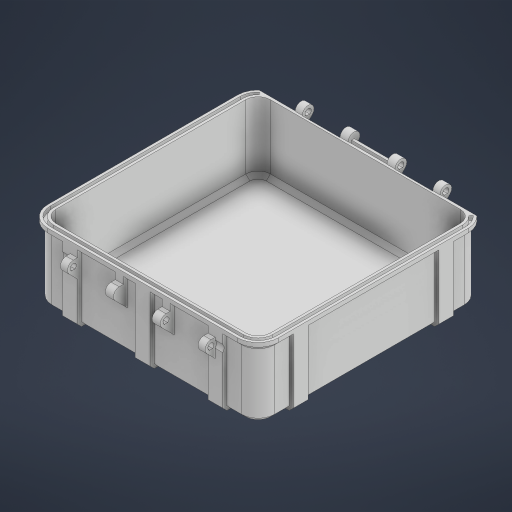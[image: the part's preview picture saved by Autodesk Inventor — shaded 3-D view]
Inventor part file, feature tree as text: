
AUTODESK INVENTOR PART (.ipt)
format: ipt  version: 2024 (Build 280153000, 153)  size: 939,520 bytes
history: native  units: mm
features: extrude x17, projected_geometry x17, sketch x11, other x9, fillet x2, chamfer x2, sweep x2, mirror x2, shell x1
ambient origin geometry x8: Origin, YZ Plane, XZ Plane, XY Plane, X Axis, Y Axis, Z Axis, Center Point
bodies: Body1 (feature_tree)
feature tree (63):
  other  "Těleso1"
  extrude  "vyska"  Depth=109.0mm
  fillet  "Zaobleni_rohu"  Radius=109.0mm
  shell  "tloustka_sten"  Thickness=35.5mm
  extrude  "vyztuhy"  Depth=8.0mm
  chamfer  "Zkoseni_spodku"  Distance=2.0mm
  sketch  "Náčrt4"
  sketch  "Náčrt3"
  sweep  "tesnici_drazka"
  sweep  "tesnici_drazka-zahloubeni"
  chamfer  "tesnici_drazka-zkoseni"  Distance=2.0mm
  other  "pant-main_nacrt"
  extrude  "Vysunutí3"  Depth=30.0mm TaperAngle=0.0deg
  extrude  "Vysunutí18"  Depth=2.0mm TaperAngle=45.0deg
  extrude  "Vysunutí4"  Depth=1.5mm
  extrude  "Vysunutí19"  Depth=2.0mm
  extrude  "Vysunutí20"  Depth=2.0mm
  other  "Pracovní rovina1"
  extrude  "Vysunutí21"  TaperAngle=0.0deg  [1 undecoded]
  extrude  "Vysunutí22"  TaperAngle=0.0deg  [1 undecoded]
  extrude  "Vysunutí23"  Depth=2.0mm TaperAngle=45.0deg
  extrude  "Vysunutí24"  Depth=3.1mm
  extrude  "Vysunutí25"  Depth=5.75mm
  extrude  "Vysunutí26"  Depth=22.0mm TaperAngle=0.0deg
  mirror  "pant-zrcadleni"
  other  "latch-main_nacrt"
  extrude  "Vysunutí14"  Depth=3.5mm TaperAngle=0.0deg
  extrude  "Vysunutí12"  Depth=18.5mm
  other  "Pracovní rovina3"
  extrude  "Vysunutí15"  Depth=3.1mm
  extrude  "Vysunutí16"  Depth=8.2mm
  mirror  "latch-zrcadleni"
  fillet  "Zaoblení2"  Radius=4.05mm
  other  "velikost"
  other  "vyztuhy-velikost"
  projected_geometry  "Promítnutá smyčka1"
  projected_geometry  "Promítnutá smyčka2"
  projected_geometry  "Promítnutá smyčka3"
  projected_geometry  "Promítnutá smyčka4"
  projected_geometry  "Promítnutá smyčka5"
  projected_geometry  "Promítnutá smyčka6"
  other  "Pracovní rovina2"
  projected_geometry  "Promítnutá smyčka16"
  sketch  "Náčrt10"
  projected_geometry  "Promítnutá smyčka17"
  sketch  "Náčrt12"
  projected_geometry  "Promítnutá smyčka18"
  other  "Pracovní rovina4"
  sketch  "Náčrt13"
  projected_geometry  "Promítnutá smyčka19"
  sketch  "Náčrt14"
  projected_geometry  "Promítnutá smyčka20"
  sketch  "Náčrt15"
  projected_geometry  "Promítnutá smyčka21"
  sketch  "Náčrt16"
  projected_geometry  "Promítnutá smyčka22"
  projected_geometry  "Promítnutá smyčka23"
  projected_geometry  "Promítnutá smyčka24"
  sketch  "Náčrt17"
  projected_geometry  "Promítnutá smyčka25"
  sketch  "Náčrt18"
  sketch  "Náčrt19"
  projected_geometry  "Promítnutá smyčka26"
note: 2 required parameter values undecoded (feature->parameter linkage not recoverable at this tier; creation-order binding heuristic only, values carry confidence <= 0.55)
